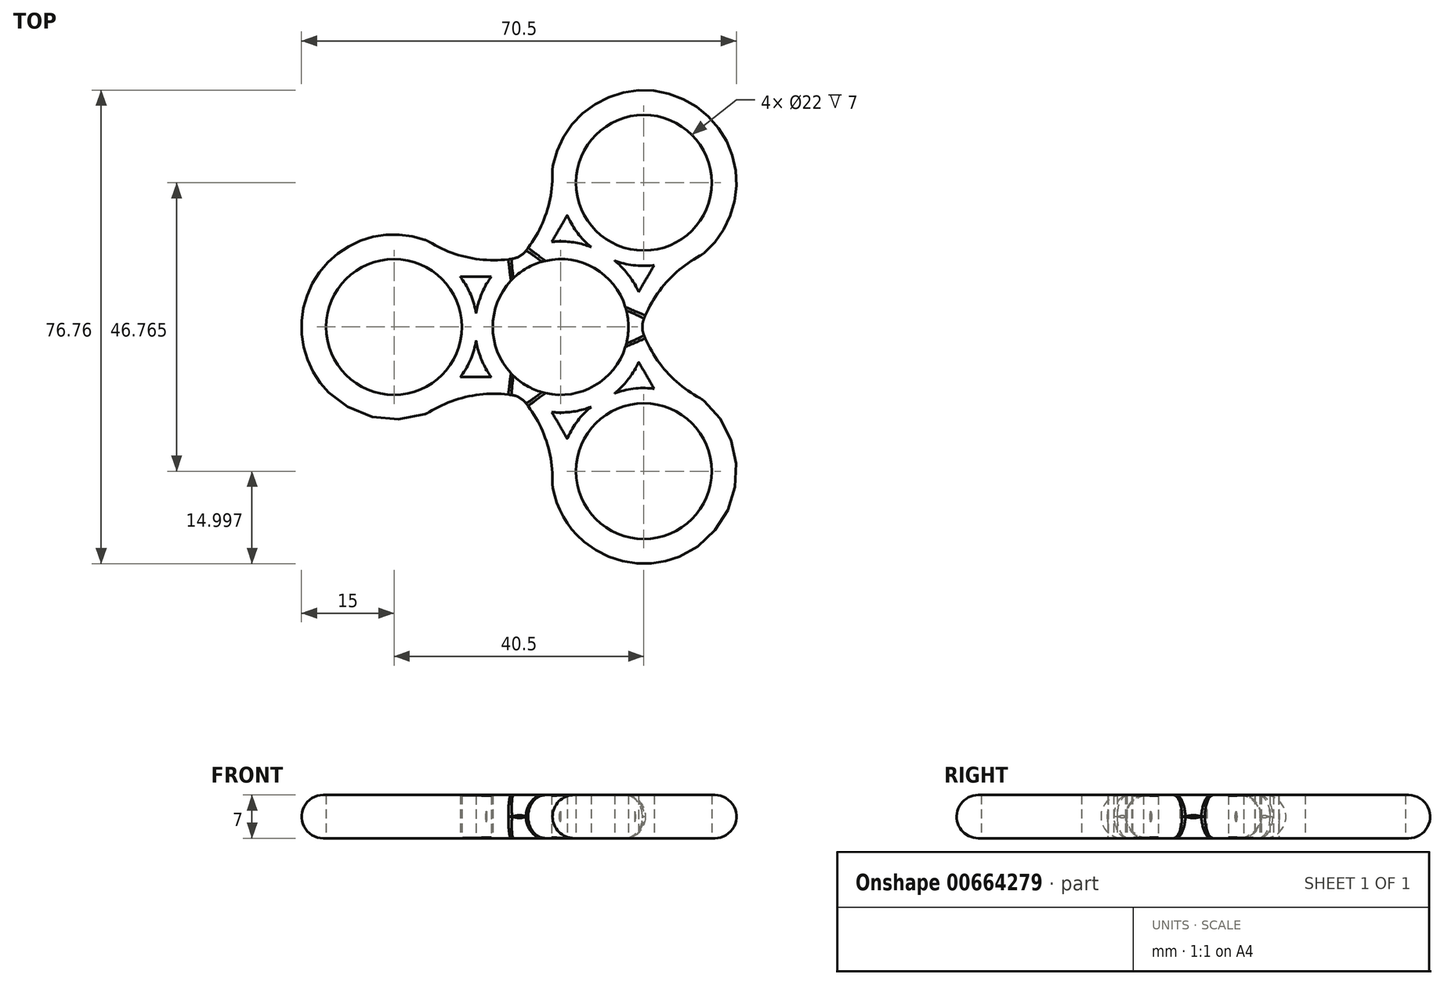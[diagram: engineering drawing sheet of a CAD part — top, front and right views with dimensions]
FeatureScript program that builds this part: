
annotation { "Feature Type Name" : "Feature", "Feature Type Description" : "" }
export const myFeature = defineFeature(function(context is Context, id is Id, definition is map)
    precondition{}
    {
        {
            var Q0;
            Q0=qCreatedBy(makeId("Front.planeOp"),FACE);
            var sketch = newSketch(context, id + "F0", { "sketchPlane" : qUnion([Q0])});
            skLineSegment(sketch, "E0", {"start": v(0, 0) * mm, "end": v(0, 6.18) * mm});
            skSolve(sketch);
        }
        {
            var Q0;
            Q0=qCreatedBy(makeId("Top.planeOp"),FACE);
            var sketch = newSketch(context, id + "F1", { "sketchPlane" : qUnion([Q0])});
            skArc(sketch, "E1", {"start": v(0, 11) * mm, "mid": v(-11, 0) * mm, "end": v(0, -11) * mm});
            skLineSegment(sketch, "E2", {"start": v(0, 56.07) * mm, "end": v(0, 11) * mm, "construction": true});
            skLineSegment(sketch, "E3", {"start": v(-42, 56.32) * mm, "end": v(-42, -55.95) * mm, "construction": true});
            skArc(sketch, "E4", {"start": v(-21.61, 14) * mm, "mid": v(-42, 0) * mm, "end": v(-21.61, -14) * mm});
            skLineSegment(sketch, "E5", {"start": v(0, 14) * mm, "end": v(0, 11) * mm});
            skLineSegment(sketch, "E6.trimOffspring", {"start": v(0, -11) * mm, "end": v(0, -55.82) * mm, "construction": true});
            skLineSegment(sketch, "E7.trimOffspring", {"start": v(0, -11) * mm, "end": v(0, -14) * mm});
            skCircle(sketch, "E8", {"center": v(-27, 0) * mm, "radius": 11 * mm});
            skArc(sketch, "E9", {"start": v(-21.61, 14) * mm, "mid": v(-10.8, 10.83) * mm, "end": v(0, 14) * mm});
            skArc(sketch, "E10", {"start": v(0, -14) * mm, "mid": v(-10.8, -10.83) * mm, "end": v(-21.61, -14) * mm});
            skArc(sketch, "E11", {"start": v(-16.24, -8.13) * mm, "mid": v(-14.6, -5.32) * mm, "end": v(-13.7, -2.2) * mm});
            skArc(sketch, "E12", {"start": v(-13.7, -2.2) * mm, "mid": v(-12.82, -5.3) * mm, "end": v(-11.24, -8.13) * mm});
            skLineSegment(sketch, "E13", {"start": v(-16.24, 8.13) * mm, "end": v(-11.24, 8.13) * mm});
            skLineSegment(sketch, "E14", {"start": v(-16.24, -8.13) * mm, "end": v(-11.24, -8.13) * mm});
            skArc(sketch, "E15.trimOffspring", {"start": v(-13.7, 2.2) * mm, "mid": v(-14.6, 5.32) * mm, "end": v(-16.24, 8.13) * mm});
            skArc(sketch, "E16.trimOffspring", {"start": v(-11.24, 8.13) * mm, "mid": v(-12.82, 5.3) * mm, "end": v(-13.7, 2.2) * mm});
            skArc(sketch, "E17.trimOffspring", {"start": v(0, 13.87) * mm, "mid": v(-0.1, 13.87) * mm, "end": v(-0.2, 13.87) * mm});
            skArc(sketch, "E18.trimOffspring", {"start": v(-0.2, -13.87) * mm, "mid": v(-0.1, -13.87) * mm, "end": v(0, -13.87) * mm});
            skSolve(sketch);
        }
        {
            var Q0;
            Q0=qSketchRegion(id+"F1",true);
            extrude(context, id + "F2", {"entities" : qUnion([Q0]), "depth" : 7 * mm, "offsetDistance" : 25 * mm});
        }
        {
            var Q0;
            Q0=makeQuery(id+"F2.opExtrude","SWEPT_BODY",BODY,{"disambiguationData":[OSD([sQuery(id+"F1.wireOp",EDGE,"E1"),sQuery(id+"F1.wireOp",EDGE,"E4"),sQuery(id+"F1.wireOp",EDGE,"FDauGuLe-8Zff-q5YO-oCp6-tykGBjxohg7e"),sQuery(id+"F1.wireOp",EDGE,"jIsLD8pJ-Ysfo-LJuf-yR93-SOJIJmbdSe7O"),sQuery(id+"F1.wireOp",EDGE,"E5"),sQuery(id+"F1.wireOp",EDGE,"E7.trimOffspring"),sQuery(id+"F1.wireOp",EDGE,"E8")])]});
            var Q1;
            Q1=sQuery(id+"F0.wireOp",EDGE,"E0");
            circularPattern(context, id + "F3", {"operationType" : NewBodyOperationType.ADD, "entities" : qUnion([Q0]), "axis" : qUnion([Q1]), "angle" : 240 * degree, "instanceCount" : 3, "equalSpace" : true});
        }
        {
            var Q0;
            Q0=makeQuery(id+"F3.boolean.opBoolean","INTERSECT",EDGE,{"derivedFrom":[makeQuery(id+"F2.opExtrude","SWEPT_FACE",FACE,{"disambiguationData":[OSD([sQuery(id+"F1.wireOp",EDGE,"E10")])]}),makeQuery(id+"F3.opPattern","COPY",FACE,{"derivedFrom":makeQuery(id+"F2.opExtrude","SWEPT_FACE",FACE,{"disambiguationData":[OSD([sQuery(id+"F1.wireOp",EDGE,"E9")])]}),"instanceName":"1"})]});
            var Q1;
            Q1=makeQuery(id+"F2.opExtrude","SWEPT_EDGE",EDGE,{"disambiguationData":[OSD([sQuery(id+"F1.wireOp",EDGE,"E4"),sQuery(id+"F1.wireOp",EDGE,"E10")])]});
            var Q2;
            Q2=makeQuery(id+"F3.opPattern","COPY",EDGE,{"derivedFrom":makeQuery(id+"F2.opExtrude","SWEPT_EDGE",EDGE,{"disambiguationData":[OSD([sQuery(id+"F1.wireOp",EDGE,"E4"),sQuery(id+"F1.wireOp",EDGE,"E9")])]}),"instanceName":"1"});
            var Q3;
            Q3=makeQuery(id+"F3.boolean.opBoolean","INTERSECT",EDGE,{"derivedFrom":[makeQuery(id+"F3.opPattern","COPY",FACE,{"derivedFrom":makeQuery(id+"F2.opExtrude","SWEPT_FACE",FACE,{"disambiguationData":[OSD([sQuery(id+"F1.wireOp",EDGE,"E10")])]}),"instanceName":"1"}),makeQuery(id+"F3.opPattern","COPY",FACE,{"derivedFrom":makeQuery(id+"F2.opExtrude","SWEPT_FACE",FACE,{"disambiguationData":[OSD([sQuery(id+"F1.wireOp",EDGE,"E9")])]}),"instanceName":"2"})]});
            var Q4;
            Q4=makeQuery(id+"F3.opPattern","COPY",EDGE,{"derivedFrom":makeQuery(id+"F2.opExtrude","SWEPT_EDGE",EDGE,{"disambiguationData":[OSD([sQuery(id+"F1.wireOp",EDGE,"E4"),sQuery(id+"F1.wireOp",EDGE,"E10")])]}),"instanceName":"1"});
            var Q5;
            Q5=makeQuery(id+"F3.opPattern","COPY",EDGE,{"derivedFrom":makeQuery(id+"F2.opExtrude","SWEPT_EDGE",EDGE,{"disambiguationData":[OSD([sQuery(id+"F1.wireOp",EDGE,"E4"),sQuery(id+"F1.wireOp",EDGE,"E9")])]}),"instanceName":"2"});
            var Q6;
            Q6=makeQuery(id+"F3.opPattern","COPY",EDGE,{"derivedFrom":makeQuery(id+"F2.opExtrude","SWEPT_EDGE",EDGE,{"disambiguationData":[OSD([sQuery(id+"F1.wireOp",EDGE,"E4"),sQuery(id+"F1.wireOp",EDGE,"E10")])]}),"instanceName":"2"});
            var Q7;
            Q7=makeQuery(id+"F3.boolean.opBoolean","INTERSECT",EDGE,{"derivedFrom":[makeQuery(id+"F2.opExtrude","SWEPT_FACE",FACE,{"disambiguationData":[OSD([sQuery(id+"F1.wireOp",EDGE,"E9")])]}),makeQuery(id+"F3.opPattern","COPY",FACE,{"derivedFrom":makeQuery(id+"F2.opExtrude","SWEPT_FACE",FACE,{"disambiguationData":[OSD([sQuery(id+"F1.wireOp",EDGE,"E10")])]}),"instanceName":"2"})]});
            var Q8;
            Q8=makeQuery(id+"F2.opExtrude","SWEPT_EDGE",EDGE,{"disambiguationData":[OSD([sQuery(id+"F1.wireOp",EDGE,"E4"),sQuery(id+"F1.wireOp",EDGE,"E9")])]});
            fillet(context, id + "F4", {"entities" : qUnion([Q0, Q1, Q2, Q3, Q4, Q5, Q6, Q7, Q8]), "radius" : 3.5 * mm, "tangentPropagation" : true, "allowEdgeOverflow" : false});
        }
        {
            var Q0;
            Q0=makeQuery(id+"F3.opPattern","COPY",EDGE,{"derivedFrom":makeQuery(id+"F2.opExtrude","CAP_EDGE",EDGE,{"disambiguationData":[OSD([sQuery(id+"F1.wireOp",EDGE,"E4")])],"isStart":false}),"instanceName":"2"});
            var Q1;
            Q1=makeQuery(id+"F3.opPattern","COPY",EDGE,{"derivedFrom":makeQuery(id+"F2.opExtrude","CAP_EDGE",EDGE,{"disambiguationData":[OSD([sQuery(id+"F1.wireOp",EDGE,"E10")])],"isStart":false}),"instanceName":"2"});
            var Q2;
            {var subQ0=sQuery(id+"F1.wireOp",EDGE,"E10");var subQ1=sQuery(id+"F1.wireOp",EDGE,"E9");var subQ2=makeQuery(id+"F2.opExtrude","CAP_FACE",FACE,{"disambiguationData":[OSD([sQuery(id+"F1.wireOp",EDGE,"E1"),sQuery(id+"F1.wireOp",EDGE,"E4"),sQuery(id+"F1.wireOp",EDGE,"E5"),sQuery(id+"F1.wireOp",EDGE,"E7.trimOffspring"),sQuery(id+"F1.wireOp",EDGE,"E8"),subQ1,subQ0])],"isStart":false});Q2=makeQuery(id+"F4.opFillet","BLEND_EDGE",EDGE,{"blendedFrom":[makeQuery(id+"F3.boolean.opBoolean","INTERSECT",EDGE,{"derivedFrom":[makeQuery(id+"F2.opExtrude","SWEPT_FACE",FACE,{"disambiguationData":[OSD([subQ1])]}),makeQuery(id+"F3.opPattern","COPY",FACE,{"derivedFrom":makeQuery(id+"F2.opExtrude","SWEPT_FACE",FACE,{"disambiguationData":[OSD([subQ0])]}),"instanceName":"2"})]}),makeQuery(id+"F3.boolean.opBoolean","MERGE",FACE,{"derivedFrom":[subQ2,makeQuery(id+"F3.opPattern","COPY",FACE,{"derivedFrom":subQ2,"instanceName":"1"}),makeQuery(id+"F3.opPattern","COPY",FACE,{"derivedFrom":subQ2,"instanceName":"2"})]})],"blendedInto":[makeQuery(id+"F3.boolean.opBoolean","MERGE",FACE,{"derivedFrom":[subQ2,makeQuery(id+"F3.opPattern","COPY",FACE,{"derivedFrom":subQ2,"instanceName":"1"}),makeQuery(id+"F3.opPattern","COPY",FACE,{"derivedFrom":subQ2,"instanceName":"2"})]})]});}
            var Q3;
            Q3=makeQuery(id+"F2.opExtrude","CAP_EDGE",EDGE,{"disambiguationData":[OSD([sQuery(id+"F1.wireOp",EDGE,"E9")])],"isStart":false});
            var Q4;
            Q4=makeQuery(id+"F2.opExtrude","CAP_EDGE",EDGE,{"disambiguationData":[OSD([sQuery(id+"F1.wireOp",EDGE,"E4")])],"isStart":false});
            var Q5;
            {var subQ0=sQuery(id+"F1.wireOp",EDGE,"E9");var subQ1=sQuery(id+"F1.wireOp",EDGE,"E4");var subQ2=makeQuery(id+"F2.opExtrude","CAP_FACE",FACE,{"disambiguationData":[OSD([sQuery(id+"F1.wireOp",EDGE,"E1"),subQ1,sQuery(id+"F1.wireOp",EDGE,"E5"),sQuery(id+"F1.wireOp",EDGE,"E7.trimOffspring"),sQuery(id+"F1.wireOp",EDGE,"E8"),subQ0,sQuery(id+"F1.wireOp",EDGE,"E10")])],"isStart":false});Q5=makeQuery(id+"F4.opFillet","BLEND_EDGE",EDGE,{"blendedFrom":[makeQuery(id+"F2.opExtrude","SWEPT_EDGE",EDGE,{"disambiguationData":[OSD([subQ1,subQ0])]}),makeQuery(id+"F3.boolean.opBoolean","MERGE",FACE,{"derivedFrom":[subQ2,makeQuery(id+"F3.opPattern","COPY",FACE,{"derivedFrom":subQ2,"instanceName":"1"}),makeQuery(id+"F3.opPattern","COPY",FACE,{"derivedFrom":subQ2,"instanceName":"2"})]})],"blendedInto":[makeQuery(id+"F3.boolean.opBoolean","MERGE",FACE,{"derivedFrom":[subQ2,makeQuery(id+"F3.opPattern","COPY",FACE,{"derivedFrom":subQ2,"instanceName":"1"}),makeQuery(id+"F3.opPattern","COPY",FACE,{"derivedFrom":subQ2,"instanceName":"2"})]})]});}
            var Q6;
            {var subQ0=sQuery(id+"F1.wireOp",EDGE,"E10");var subQ1=sQuery(id+"F1.wireOp",EDGE,"E4");var subQ2=makeQuery(id+"F2.opExtrude","CAP_FACE",FACE,{"disambiguationData":[OSD([sQuery(id+"F1.wireOp",EDGE,"E1"),subQ1,sQuery(id+"F1.wireOp",EDGE,"E5"),sQuery(id+"F1.wireOp",EDGE,"E7.trimOffspring"),sQuery(id+"F1.wireOp",EDGE,"E8"),sQuery(id+"F1.wireOp",EDGE,"E9"),subQ0])],"isStart":false});Q6=makeQuery(id+"F4.opFillet","BLEND_EDGE",EDGE,{"blendedFrom":[makeQuery(id+"F3.opPattern","COPY",EDGE,{"derivedFrom":makeQuery(id+"F2.opExtrude","SWEPT_EDGE",EDGE,{"disambiguationData":[OSD([subQ1,subQ0])]}),"instanceName":"2"}),makeQuery(id+"F3.boolean.opBoolean","MERGE",FACE,{"derivedFrom":[subQ2,makeQuery(id+"F3.opPattern","COPY",FACE,{"derivedFrom":subQ2,"instanceName":"1"}),makeQuery(id+"F3.opPattern","COPY",FACE,{"derivedFrom":subQ2,"instanceName":"2"})]})],"blendedInto":[makeQuery(id+"F3.boolean.opBoolean","MERGE",FACE,{"derivedFrom":[subQ2,makeQuery(id+"F3.opPattern","COPY",FACE,{"derivedFrom":subQ2,"instanceName":"1"}),makeQuery(id+"F3.opPattern","COPY",FACE,{"derivedFrom":subQ2,"instanceName":"2"})]})]});}
            var Q7;
            Q7=makeQuery(id+"F3.opPattern","COPY",EDGE,{"derivedFrom":makeQuery(id+"F2.opExtrude","CAP_EDGE",EDGE,{"disambiguationData":[OSD([sQuery(id+"F1.wireOp",EDGE,"E10")])],"isStart":false}),"instanceName":"1"});
            var Q8;
            {var subQ0=sQuery(id+"F1.wireOp",EDGE,"E10");var subQ1=sQuery(id+"F1.wireOp",EDGE,"E4");var subQ2=makeQuery(id+"F2.opExtrude","CAP_FACE",FACE,{"disambiguationData":[OSD([sQuery(id+"F1.wireOp",EDGE,"E1"),subQ1,sQuery(id+"F1.wireOp",EDGE,"E5"),sQuery(id+"F1.wireOp",EDGE,"E7.trimOffspring"),sQuery(id+"F1.wireOp",EDGE,"E8"),sQuery(id+"F1.wireOp",EDGE,"E9"),subQ0])],"isStart":false});Q8=makeQuery(id+"F4.opFillet","BLEND_EDGE",EDGE,{"blendedFrom":[makeQuery(id+"F3.opPattern","COPY",EDGE,{"derivedFrom":makeQuery(id+"F2.opExtrude","SWEPT_EDGE",EDGE,{"disambiguationData":[OSD([subQ1,subQ0])]}),"instanceName":"1"}),makeQuery(id+"F3.boolean.opBoolean","MERGE",FACE,{"derivedFrom":[subQ2,makeQuery(id+"F3.opPattern","COPY",FACE,{"derivedFrom":subQ2,"instanceName":"1"}),makeQuery(id+"F3.opPattern","COPY",FACE,{"derivedFrom":subQ2,"instanceName":"2"})]})],"blendedInto":[makeQuery(id+"F3.boolean.opBoolean","MERGE",FACE,{"derivedFrom":[subQ2,makeQuery(id+"F3.opPattern","COPY",FACE,{"derivedFrom":subQ2,"instanceName":"1"}),makeQuery(id+"F3.opPattern","COPY",FACE,{"derivedFrom":subQ2,"instanceName":"2"})]})]});}
            var Q9;
            Q9=makeQuery(id+"F3.opPattern","COPY",EDGE,{"derivedFrom":makeQuery(id+"F2.opExtrude","CAP_EDGE",EDGE,{"disambiguationData":[OSD([sQuery(id+"F1.wireOp",EDGE,"E4")])],"isStart":false}),"instanceName":"1"});
            var Q10;
            {var subQ0=sQuery(id+"F1.wireOp",EDGE,"E10");var subQ1=sQuery(id+"F1.wireOp",EDGE,"E9");var subQ2=makeQuery(id+"F2.opExtrude","CAP_FACE",FACE,{"disambiguationData":[OSD([sQuery(id+"F1.wireOp",EDGE,"E1"),sQuery(id+"F1.wireOp",EDGE,"E4"),sQuery(id+"F1.wireOp",EDGE,"E5"),sQuery(id+"F1.wireOp",EDGE,"E7.trimOffspring"),sQuery(id+"F1.wireOp",EDGE,"E8"),subQ1,subQ0])],"isStart":false});Q10=makeQuery(id+"F4.opFillet","BLEND_EDGE",EDGE,{"blendedFrom":[makeQuery(id+"F3.boolean.opBoolean","INTERSECT",EDGE,{"derivedFrom":[makeQuery(id+"F3.opPattern","COPY",FACE,{"derivedFrom":makeQuery(id+"F2.opExtrude","SWEPT_FACE",FACE,{"disambiguationData":[OSD([subQ0])]}),"instanceName":"1"}),makeQuery(id+"F3.opPattern","COPY",FACE,{"derivedFrom":makeQuery(id+"F2.opExtrude","SWEPT_FACE",FACE,{"disambiguationData":[OSD([subQ1])]}),"instanceName":"2"})]}),makeQuery(id+"F3.boolean.opBoolean","MERGE",FACE,{"derivedFrom":[subQ2,makeQuery(id+"F3.opPattern","COPY",FACE,{"derivedFrom":subQ2,"instanceName":"1"}),makeQuery(id+"F3.opPattern","COPY",FACE,{"derivedFrom":subQ2,"instanceName":"2"})]})],"blendedInto":[makeQuery(id+"F3.boolean.opBoolean","MERGE",FACE,{"derivedFrom":[subQ2,makeQuery(id+"F3.opPattern","COPY",FACE,{"derivedFrom":subQ2,"instanceName":"1"}),makeQuery(id+"F3.opPattern","COPY",FACE,{"derivedFrom":subQ2,"instanceName":"2"})]})]});}
            var Q11;
            Q11=makeQuery(id+"F3.opPattern","COPY",EDGE,{"derivedFrom":makeQuery(id+"F2.opExtrude","CAP_EDGE",EDGE,{"disambiguationData":[OSD([sQuery(id+"F1.wireOp",EDGE,"E9")])],"isStart":false}),"instanceName":"2"});
            var Q12;
            {var subQ0=sQuery(id+"F1.wireOp",EDGE,"E9");var subQ1=sQuery(id+"F1.wireOp",EDGE,"E4");var subQ2=makeQuery(id+"F2.opExtrude","CAP_FACE",FACE,{"disambiguationData":[OSD([sQuery(id+"F1.wireOp",EDGE,"E1"),subQ1,sQuery(id+"F1.wireOp",EDGE,"E5"),sQuery(id+"F1.wireOp",EDGE,"E7.trimOffspring"),sQuery(id+"F1.wireOp",EDGE,"E8"),subQ0,sQuery(id+"F1.wireOp",EDGE,"E10")])],"isStart":false});Q12=makeQuery(id+"F4.opFillet","BLEND_EDGE",EDGE,{"blendedFrom":[makeQuery(id+"F3.opPattern","COPY",EDGE,{"derivedFrom":makeQuery(id+"F2.opExtrude","SWEPT_EDGE",EDGE,{"disambiguationData":[OSD([subQ1,subQ0])]}),"instanceName":"2"}),makeQuery(id+"F3.boolean.opBoolean","MERGE",FACE,{"derivedFrom":[subQ2,makeQuery(id+"F3.opPattern","COPY",FACE,{"derivedFrom":subQ2,"instanceName":"1"}),makeQuery(id+"F3.opPattern","COPY",FACE,{"derivedFrom":subQ2,"instanceName":"2"})]})],"blendedInto":[makeQuery(id+"F3.boolean.opBoolean","MERGE",FACE,{"derivedFrom":[subQ2,makeQuery(id+"F3.opPattern","COPY",FACE,{"derivedFrom":subQ2,"instanceName":"1"}),makeQuery(id+"F3.opPattern","COPY",FACE,{"derivedFrom":subQ2,"instanceName":"2"})]})]});}
            var Q13;
            Q13=makeQuery(id+"F3.opPattern","COPY",EDGE,{"derivedFrom":makeQuery(id+"F2.opExtrude","CAP_EDGE",EDGE,{"disambiguationData":[OSD([sQuery(id+"F1.wireOp",EDGE,"E9")])],"isStart":false}),"instanceName":"1"});
            var Q14;
            {var subQ0=sQuery(id+"F1.wireOp",EDGE,"E9");var subQ1=sQuery(id+"F1.wireOp",EDGE,"E4");var subQ2=makeQuery(id+"F2.opExtrude","CAP_FACE",FACE,{"disambiguationData":[OSD([sQuery(id+"F1.wireOp",EDGE,"E1"),subQ1,sQuery(id+"F1.wireOp",EDGE,"E5"),sQuery(id+"F1.wireOp",EDGE,"E7.trimOffspring"),sQuery(id+"F1.wireOp",EDGE,"E8"),subQ0,sQuery(id+"F1.wireOp",EDGE,"E10")])],"isStart":false});Q14=makeQuery(id+"F4.opFillet","BLEND_EDGE",EDGE,{"blendedFrom":[makeQuery(id+"F3.opPattern","COPY",EDGE,{"derivedFrom":makeQuery(id+"F2.opExtrude","SWEPT_EDGE",EDGE,{"disambiguationData":[OSD([subQ1,subQ0])]}),"instanceName":"1"}),makeQuery(id+"F3.boolean.opBoolean","MERGE",FACE,{"derivedFrom":[subQ2,makeQuery(id+"F3.opPattern","COPY",FACE,{"derivedFrom":subQ2,"instanceName":"1"}),makeQuery(id+"F3.opPattern","COPY",FACE,{"derivedFrom":subQ2,"instanceName":"2"})]})],"blendedInto":[makeQuery(id+"F3.boolean.opBoolean","MERGE",FACE,{"derivedFrom":[subQ2,makeQuery(id+"F3.opPattern","COPY",FACE,{"derivedFrom":subQ2,"instanceName":"1"}),makeQuery(id+"F3.opPattern","COPY",FACE,{"derivedFrom":subQ2,"instanceName":"2"})]})]});}
            var Q15;
            Q15=makeQuery(id+"F2.opExtrude","CAP_EDGE",EDGE,{"disambiguationData":[OSD([sQuery(id+"F1.wireOp",EDGE,"E10")])],"isStart":false});
            var Q16;
            {var subQ0=sQuery(id+"F1.wireOp",EDGE,"E10");var subQ1=sQuery(id+"F1.wireOp",EDGE,"E4");var subQ2=makeQuery(id+"F2.opExtrude","CAP_FACE",FACE,{"disambiguationData":[OSD([sQuery(id+"F1.wireOp",EDGE,"E1"),subQ1,sQuery(id+"F1.wireOp",EDGE,"E5"),sQuery(id+"F1.wireOp",EDGE,"E7.trimOffspring"),sQuery(id+"F1.wireOp",EDGE,"E8"),sQuery(id+"F1.wireOp",EDGE,"E9"),subQ0])],"isStart":false});Q16=makeQuery(id+"F4.opFillet","BLEND_EDGE",EDGE,{"blendedFrom":[makeQuery(id+"F2.opExtrude","SWEPT_EDGE",EDGE,{"disambiguationData":[OSD([subQ1,subQ0])]}),makeQuery(id+"F3.boolean.opBoolean","MERGE",FACE,{"derivedFrom":[subQ2,makeQuery(id+"F3.opPattern","COPY",FACE,{"derivedFrom":subQ2,"instanceName":"1"}),makeQuery(id+"F3.opPattern","COPY",FACE,{"derivedFrom":subQ2,"instanceName":"2"})]})],"blendedInto":[makeQuery(id+"F3.boolean.opBoolean","MERGE",FACE,{"derivedFrom":[subQ2,makeQuery(id+"F3.opPattern","COPY",FACE,{"derivedFrom":subQ2,"instanceName":"1"}),makeQuery(id+"F3.opPattern","COPY",FACE,{"derivedFrom":subQ2,"instanceName":"2"})]})]});}
            var Q17;
            {var subQ0=sQuery(id+"F1.wireOp",EDGE,"E10");var subQ1=sQuery(id+"F1.wireOp",EDGE,"E9");var subQ2=makeQuery(id+"F2.opExtrude","CAP_FACE",FACE,{"disambiguationData":[OSD([sQuery(id+"F1.wireOp",EDGE,"E1"),sQuery(id+"F1.wireOp",EDGE,"E4"),sQuery(id+"F1.wireOp",EDGE,"E5"),sQuery(id+"F1.wireOp",EDGE,"E7.trimOffspring"),sQuery(id+"F1.wireOp",EDGE,"E8"),subQ1,subQ0])],"isStart":false});Q17=makeQuery(id+"F4.opFillet","BLEND_EDGE",EDGE,{"blendedFrom":[makeQuery(id+"F3.boolean.opBoolean","INTERSECT",EDGE,{"derivedFrom":[makeQuery(id+"F2.opExtrude","SWEPT_FACE",FACE,{"disambiguationData":[OSD([subQ0])]}),makeQuery(id+"F3.opPattern","COPY",FACE,{"derivedFrom":makeQuery(id+"F2.opExtrude","SWEPT_FACE",FACE,{"disambiguationData":[OSD([subQ1])]}),"instanceName":"1"})]}),makeQuery(id+"F3.boolean.opBoolean","MERGE",FACE,{"derivedFrom":[subQ2,makeQuery(id+"F3.opPattern","COPY",FACE,{"derivedFrom":subQ2,"instanceName":"1"}),makeQuery(id+"F3.opPattern","COPY",FACE,{"derivedFrom":subQ2,"instanceName":"2"})]})],"blendedInto":[makeQuery(id+"F3.boolean.opBoolean","MERGE",FACE,{"derivedFrom":[subQ2,makeQuery(id+"F3.opPattern","COPY",FACE,{"derivedFrom":subQ2,"instanceName":"1"}),makeQuery(id+"F3.opPattern","COPY",FACE,{"derivedFrom":subQ2,"instanceName":"2"})]})]});}
            fillet(context, id + "F5", {"entities" : qUnion([Q0, Q1, Q2, Q3, Q4, Q5, Q6, Q7, Q8, Q9, Q10, Q11, Q12, Q13, Q14, Q15, Q16, Q17]), "radius" : 3.5 * mm, "tangentPropagation" : true, "allowEdgeOverflow" : false});
        }
        {
            var Q0;
            Q0=makeQuery(id+"F3.opPattern","COPY",EDGE,{"derivedFrom":makeQuery(id+"F2.opExtrude","CAP_EDGE",EDGE,{"disambiguationData":[OSD([sQuery(id+"F1.wireOp",EDGE,"E4")])],"isStart":true}),"instanceName":"1"});
            var Q1;
            Q1=makeQuery(id+"F3.opPattern","COPY",EDGE,{"derivedFrom":makeQuery(id+"F2.opExtrude","CAP_EDGE",EDGE,{"disambiguationData":[OSD([sQuery(id+"F1.wireOp",EDGE,"E4")])],"isStart":true}),"instanceName":"2"});
            var Q2;
            Q2=makeQuery(id+"F2.opExtrude","CAP_EDGE",EDGE,{"disambiguationData":[OSD([sQuery(id+"F1.wireOp",EDGE,"E4")])],"isStart":true});
            var Q3;
            Q3=makeQuery(id+"F2.opExtrude","CAP_EDGE",EDGE,{"disambiguationData":[OSD([sQuery(id+"F1.wireOp",EDGE,"E10")])],"isStart":true});
            var Q4;
            Q4=makeQuery(id+"F3.opPattern","COPY",EDGE,{"derivedFrom":makeQuery(id+"F2.opExtrude","CAP_EDGE",EDGE,{"disambiguationData":[OSD([sQuery(id+"F1.wireOp",EDGE,"E9")])],"isStart":true}),"instanceName":"1"});
            var Q5;
            Q5=makeQuery(id+"F3.opPattern","COPY",EDGE,{"derivedFrom":makeQuery(id+"F2.opExtrude","CAP_EDGE",EDGE,{"disambiguationData":[OSD([sQuery(id+"F1.wireOp",EDGE,"E10")])],"isStart":true}),"instanceName":"1"});
            var Q6;
            Q6=makeQuery(id+"F3.opPattern","COPY",EDGE,{"derivedFrom":makeQuery(id+"F2.opExtrude","CAP_EDGE",EDGE,{"disambiguationData":[OSD([sQuery(id+"F1.wireOp",EDGE,"E10")])],"isStart":true}),"instanceName":"2"});
            var Q7;
            Q7=makeQuery(id+"F2.opExtrude","CAP_EDGE",EDGE,{"disambiguationData":[OSD([sQuery(id+"F1.wireOp",EDGE,"E9")])],"isStart":true});
            var Q8;
            {var subQ0=sQuery(id+"F1.wireOp",EDGE,"E10");var subQ1=sQuery(id+"F1.wireOp",EDGE,"E9");var subQ2=makeQuery(id+"F2.opExtrude","CAP_FACE",FACE,{"disambiguationData":[OSD([sQuery(id+"F1.wireOp",EDGE,"E1"),sQuery(id+"F1.wireOp",EDGE,"E4"),sQuery(id+"F1.wireOp",EDGE,"E5"),sQuery(id+"F1.wireOp",EDGE,"E7.trimOffspring"),sQuery(id+"F1.wireOp",EDGE,"E8"),subQ1,subQ0])],"isStart":true});Q8=makeQuery(id+"F4.opFillet","BLEND_EDGE",EDGE,{"blendedFrom":[makeQuery(id+"F3.boolean.opBoolean","INTERSECT",EDGE,{"derivedFrom":[makeQuery(id+"F2.opExtrude","SWEPT_FACE",FACE,{"disambiguationData":[OSD([subQ1])]}),makeQuery(id+"F3.opPattern","COPY",FACE,{"derivedFrom":makeQuery(id+"F2.opExtrude","SWEPT_FACE",FACE,{"disambiguationData":[OSD([subQ0])]}),"instanceName":"2"})]}),makeQuery(id+"F3.boolean.opBoolean","MERGE",FACE,{"derivedFrom":[subQ2,makeQuery(id+"F3.opPattern","COPY",FACE,{"derivedFrom":subQ2,"instanceName":"1"}),makeQuery(id+"F3.opPattern","COPY",FACE,{"derivedFrom":subQ2,"instanceName":"2"})]})],"blendedInto":[makeQuery(id+"F3.boolean.opBoolean","MERGE",FACE,{"derivedFrom":[subQ2,makeQuery(id+"F3.opPattern","COPY",FACE,{"derivedFrom":subQ2,"instanceName":"1"}),makeQuery(id+"F3.opPattern","COPY",FACE,{"derivedFrom":subQ2,"instanceName":"2"})]})]});}
            var Q9;
            {var subQ0=sQuery(id+"F1.wireOp",EDGE,"E10");var subQ1=sQuery(id+"F1.wireOp",EDGE,"E9");var subQ2=makeQuery(id+"F2.opExtrude","CAP_FACE",FACE,{"disambiguationData":[OSD([sQuery(id+"F1.wireOp",EDGE,"E1"),sQuery(id+"F1.wireOp",EDGE,"E4"),sQuery(id+"F1.wireOp",EDGE,"E5"),sQuery(id+"F1.wireOp",EDGE,"E7.trimOffspring"),sQuery(id+"F1.wireOp",EDGE,"E8"),subQ1,subQ0])],"isStart":true});Q9=makeQuery(id+"F4.opFillet","BLEND_EDGE",EDGE,{"blendedFrom":[makeQuery(id+"F3.boolean.opBoolean","INTERSECT",EDGE,{"derivedFrom":[makeQuery(id+"F2.opExtrude","SWEPT_FACE",FACE,{"disambiguationData":[OSD([subQ0])]}),makeQuery(id+"F3.opPattern","COPY",FACE,{"derivedFrom":makeQuery(id+"F2.opExtrude","SWEPT_FACE",FACE,{"disambiguationData":[OSD([subQ1])]}),"instanceName":"1"})]}),makeQuery(id+"F3.boolean.opBoolean","MERGE",FACE,{"derivedFrom":[subQ2,makeQuery(id+"F3.opPattern","COPY",FACE,{"derivedFrom":subQ2,"instanceName":"1"}),makeQuery(id+"F3.opPattern","COPY",FACE,{"derivedFrom":subQ2,"instanceName":"2"})]})],"blendedInto":[makeQuery(id+"F3.boolean.opBoolean","MERGE",FACE,{"derivedFrom":[subQ2,makeQuery(id+"F3.opPattern","COPY",FACE,{"derivedFrom":subQ2,"instanceName":"1"}),makeQuery(id+"F3.opPattern","COPY",FACE,{"derivedFrom":subQ2,"instanceName":"2"})]})]});}
            var Q10;
            {var subQ0=sQuery(id+"F1.wireOp",EDGE,"E10");var subQ1=sQuery(id+"F1.wireOp",EDGE,"E4");var subQ2=makeQuery(id+"F2.opExtrude","CAP_FACE",FACE,{"disambiguationData":[OSD([sQuery(id+"F1.wireOp",EDGE,"E1"),subQ1,sQuery(id+"F1.wireOp",EDGE,"E5"),sQuery(id+"F1.wireOp",EDGE,"E7.trimOffspring"),sQuery(id+"F1.wireOp",EDGE,"E8"),sQuery(id+"F1.wireOp",EDGE,"E9"),subQ0])],"isStart":true});Q10=makeQuery(id+"F4.opFillet","BLEND_EDGE",EDGE,{"blendedFrom":[makeQuery(id+"F2.opExtrude","SWEPT_EDGE",EDGE,{"disambiguationData":[OSD([subQ1,subQ0])]}),makeQuery(id+"F3.boolean.opBoolean","MERGE",FACE,{"derivedFrom":[subQ2,makeQuery(id+"F3.opPattern","COPY",FACE,{"derivedFrom":subQ2,"instanceName":"1"}),makeQuery(id+"F3.opPattern","COPY",FACE,{"derivedFrom":subQ2,"instanceName":"2"})]})],"blendedInto":[makeQuery(id+"F3.boolean.opBoolean","MERGE",FACE,{"derivedFrom":[subQ2,makeQuery(id+"F3.opPattern","COPY",FACE,{"derivedFrom":subQ2,"instanceName":"1"}),makeQuery(id+"F3.opPattern","COPY",FACE,{"derivedFrom":subQ2,"instanceName":"2"})]})]});}
            var Q11;
            {var subQ0=sQuery(id+"F1.wireOp",EDGE,"E9");var subQ1=sQuery(id+"F1.wireOp",EDGE,"E4");var subQ2=makeQuery(id+"F2.opExtrude","CAP_FACE",FACE,{"disambiguationData":[OSD([sQuery(id+"F1.wireOp",EDGE,"E1"),subQ1,sQuery(id+"F1.wireOp",EDGE,"E5"),sQuery(id+"F1.wireOp",EDGE,"E7.trimOffspring"),sQuery(id+"F1.wireOp",EDGE,"E8"),subQ0,sQuery(id+"F1.wireOp",EDGE,"E10")])],"isStart":true});Q11=makeQuery(id+"F4.opFillet","BLEND_EDGE",EDGE,{"blendedFrom":[makeQuery(id+"F2.opExtrude","SWEPT_EDGE",EDGE,{"disambiguationData":[OSD([subQ1,subQ0])]}),makeQuery(id+"F3.boolean.opBoolean","MERGE",FACE,{"derivedFrom":[subQ2,makeQuery(id+"F3.opPattern","COPY",FACE,{"derivedFrom":subQ2,"instanceName":"1"}),makeQuery(id+"F3.opPattern","COPY",FACE,{"derivedFrom":subQ2,"instanceName":"2"})]})],"blendedInto":[makeQuery(id+"F3.boolean.opBoolean","MERGE",FACE,{"derivedFrom":[subQ2,makeQuery(id+"F3.opPattern","COPY",FACE,{"derivedFrom":subQ2,"instanceName":"1"}),makeQuery(id+"F3.opPattern","COPY",FACE,{"derivedFrom":subQ2,"instanceName":"2"})]})]});}
            var Q12;
            {var subQ0=sQuery(id+"F1.wireOp",EDGE,"E10");var subQ1=sQuery(id+"F1.wireOp",EDGE,"E4");var subQ2=makeQuery(id+"F2.opExtrude","CAP_FACE",FACE,{"disambiguationData":[OSD([sQuery(id+"F1.wireOp",EDGE,"E1"),subQ1,sQuery(id+"F1.wireOp",EDGE,"E5"),sQuery(id+"F1.wireOp",EDGE,"E7.trimOffspring"),sQuery(id+"F1.wireOp",EDGE,"E8"),sQuery(id+"F1.wireOp",EDGE,"E9"),subQ0])],"isStart":true});Q12=makeQuery(id+"F4.opFillet","BLEND_EDGE",EDGE,{"blendedFrom":[makeQuery(id+"F3.opPattern","COPY",EDGE,{"derivedFrom":makeQuery(id+"F2.opExtrude","SWEPT_EDGE",EDGE,{"disambiguationData":[OSD([subQ1,subQ0])]}),"instanceName":"2"}),makeQuery(id+"F3.boolean.opBoolean","MERGE",FACE,{"derivedFrom":[subQ2,makeQuery(id+"F3.opPattern","COPY",FACE,{"derivedFrom":subQ2,"instanceName":"1"}),makeQuery(id+"F3.opPattern","COPY",FACE,{"derivedFrom":subQ2,"instanceName":"2"})]})],"blendedInto":[makeQuery(id+"F3.boolean.opBoolean","MERGE",FACE,{"derivedFrom":[subQ2,makeQuery(id+"F3.opPattern","COPY",FACE,{"derivedFrom":subQ2,"instanceName":"1"}),makeQuery(id+"F3.opPattern","COPY",FACE,{"derivedFrom":subQ2,"instanceName":"2"})]})]});}
            var Q13;
            Q13=makeQuery(id+"F3.opPattern","COPY",EDGE,{"derivedFrom":makeQuery(id+"F2.opExtrude","CAP_EDGE",EDGE,{"disambiguationData":[OSD([sQuery(id+"F1.wireOp",EDGE,"E9")])],"isStart":true}),"instanceName":"2"});
            var Q14;
            {var subQ0=sQuery(id+"F1.wireOp",EDGE,"E9");var subQ1=sQuery(id+"F1.wireOp",EDGE,"E4");var subQ2=makeQuery(id+"F2.opExtrude","CAP_FACE",FACE,{"disambiguationData":[OSD([sQuery(id+"F1.wireOp",EDGE,"E1"),subQ1,sQuery(id+"F1.wireOp",EDGE,"E5"),sQuery(id+"F1.wireOp",EDGE,"E7.trimOffspring"),sQuery(id+"F1.wireOp",EDGE,"E8"),subQ0,sQuery(id+"F1.wireOp",EDGE,"E10")])],"isStart":true});Q14=makeQuery(id+"F4.opFillet","BLEND_EDGE",EDGE,{"blendedFrom":[makeQuery(id+"F3.opPattern","COPY",EDGE,{"derivedFrom":makeQuery(id+"F2.opExtrude","SWEPT_EDGE",EDGE,{"disambiguationData":[OSD([subQ1,subQ0])]}),"instanceName":"2"}),makeQuery(id+"F3.boolean.opBoolean","MERGE",FACE,{"derivedFrom":[subQ2,makeQuery(id+"F3.opPattern","COPY",FACE,{"derivedFrom":subQ2,"instanceName":"1"}),makeQuery(id+"F3.opPattern","COPY",FACE,{"derivedFrom":subQ2,"instanceName":"2"})]})],"blendedInto":[makeQuery(id+"F3.boolean.opBoolean","MERGE",FACE,{"derivedFrom":[subQ2,makeQuery(id+"F3.opPattern","COPY",FACE,{"derivedFrom":subQ2,"instanceName":"1"}),makeQuery(id+"F3.opPattern","COPY",FACE,{"derivedFrom":subQ2,"instanceName":"2"})]})]});}
            var Q15;
            {var subQ0=sQuery(id+"F1.wireOp",EDGE,"E10");var subQ1=sQuery(id+"F1.wireOp",EDGE,"E9");var subQ2=makeQuery(id+"F2.opExtrude","CAP_FACE",FACE,{"disambiguationData":[OSD([sQuery(id+"F1.wireOp",EDGE,"E1"),sQuery(id+"F1.wireOp",EDGE,"E4"),sQuery(id+"F1.wireOp",EDGE,"E5"),sQuery(id+"F1.wireOp",EDGE,"E7.trimOffspring"),sQuery(id+"F1.wireOp",EDGE,"E8"),subQ1,subQ0])],"isStart":true});Q15=makeQuery(id+"F4.opFillet","BLEND_EDGE",EDGE,{"blendedFrom":[makeQuery(id+"F3.boolean.opBoolean","INTERSECT",EDGE,{"derivedFrom":[makeQuery(id+"F3.opPattern","COPY",FACE,{"derivedFrom":makeQuery(id+"F2.opExtrude","SWEPT_FACE",FACE,{"disambiguationData":[OSD([subQ0])]}),"instanceName":"1"}),makeQuery(id+"F3.opPattern","COPY",FACE,{"derivedFrom":makeQuery(id+"F2.opExtrude","SWEPT_FACE",FACE,{"disambiguationData":[OSD([subQ1])]}),"instanceName":"2"})]}),makeQuery(id+"F3.boolean.opBoolean","MERGE",FACE,{"derivedFrom":[subQ2,makeQuery(id+"F3.opPattern","COPY",FACE,{"derivedFrom":subQ2,"instanceName":"1"}),makeQuery(id+"F3.opPattern","COPY",FACE,{"derivedFrom":subQ2,"instanceName":"2"})]})],"blendedInto":[makeQuery(id+"F3.boolean.opBoolean","MERGE",FACE,{"derivedFrom":[subQ2,makeQuery(id+"F3.opPattern","COPY",FACE,{"derivedFrom":subQ2,"instanceName":"1"}),makeQuery(id+"F3.opPattern","COPY",FACE,{"derivedFrom":subQ2,"instanceName":"2"})]})]});}
            var Q16;
            {var subQ0=sQuery(id+"F1.wireOp",EDGE,"E10");var subQ1=sQuery(id+"F1.wireOp",EDGE,"E4");var subQ2=makeQuery(id+"F2.opExtrude","CAP_FACE",FACE,{"disambiguationData":[OSD([sQuery(id+"F1.wireOp",EDGE,"E1"),subQ1,sQuery(id+"F1.wireOp",EDGE,"E5"),sQuery(id+"F1.wireOp",EDGE,"E7.trimOffspring"),sQuery(id+"F1.wireOp",EDGE,"E8"),sQuery(id+"F1.wireOp",EDGE,"E9"),subQ0])],"isStart":true});Q16=makeQuery(id+"F4.opFillet","BLEND_EDGE",EDGE,{"blendedFrom":[makeQuery(id+"F3.opPattern","COPY",EDGE,{"derivedFrom":makeQuery(id+"F2.opExtrude","SWEPT_EDGE",EDGE,{"disambiguationData":[OSD([subQ1,subQ0])]}),"instanceName":"1"}),makeQuery(id+"F3.boolean.opBoolean","MERGE",FACE,{"derivedFrom":[subQ2,makeQuery(id+"F3.opPattern","COPY",FACE,{"derivedFrom":subQ2,"instanceName":"1"}),makeQuery(id+"F3.opPattern","COPY",FACE,{"derivedFrom":subQ2,"instanceName":"2"})]})],"blendedInto":[makeQuery(id+"F3.boolean.opBoolean","MERGE",FACE,{"derivedFrom":[subQ2,makeQuery(id+"F3.opPattern","COPY",FACE,{"derivedFrom":subQ2,"instanceName":"1"}),makeQuery(id+"F3.opPattern","COPY",FACE,{"derivedFrom":subQ2,"instanceName":"2"})]})]});}
            var Q17;
            {var subQ0=sQuery(id+"F1.wireOp",EDGE,"E9");var subQ1=sQuery(id+"F1.wireOp",EDGE,"E4");var subQ2=makeQuery(id+"F2.opExtrude","CAP_FACE",FACE,{"disambiguationData":[OSD([sQuery(id+"F1.wireOp",EDGE,"E1"),subQ1,sQuery(id+"F1.wireOp",EDGE,"E5"),sQuery(id+"F1.wireOp",EDGE,"E7.trimOffspring"),sQuery(id+"F1.wireOp",EDGE,"E8"),subQ0,sQuery(id+"F1.wireOp",EDGE,"E10")])],"isStart":true});Q17=makeQuery(id+"F4.opFillet","BLEND_EDGE",EDGE,{"blendedFrom":[makeQuery(id+"F3.opPattern","COPY",EDGE,{"derivedFrom":makeQuery(id+"F2.opExtrude","SWEPT_EDGE",EDGE,{"disambiguationData":[OSD([subQ1,subQ0])]}),"instanceName":"1"}),makeQuery(id+"F3.boolean.opBoolean","MERGE",FACE,{"derivedFrom":[subQ2,makeQuery(id+"F3.opPattern","COPY",FACE,{"derivedFrom":subQ2,"instanceName":"1"}),makeQuery(id+"F3.opPattern","COPY",FACE,{"derivedFrom":subQ2,"instanceName":"2"})]})],"blendedInto":[makeQuery(id+"F3.boolean.opBoolean","MERGE",FACE,{"derivedFrom":[subQ2,makeQuery(id+"F3.opPattern","COPY",FACE,{"derivedFrom":subQ2,"instanceName":"1"}),makeQuery(id+"F3.opPattern","COPY",FACE,{"derivedFrom":subQ2,"instanceName":"2"})]})]});}
            fillet(context, id + "F6", {"entities" : qUnion([Q0, Q1, Q2, Q3, Q4, Q5, Q6, Q7, Q8, Q9, Q10, Q11, Q12, Q13, Q14, Q15, Q16, Q17]), "radius" : 3.5 * mm, "tangentPropagation" : true, "allowEdgeOverflow" : false});
        }
    });
